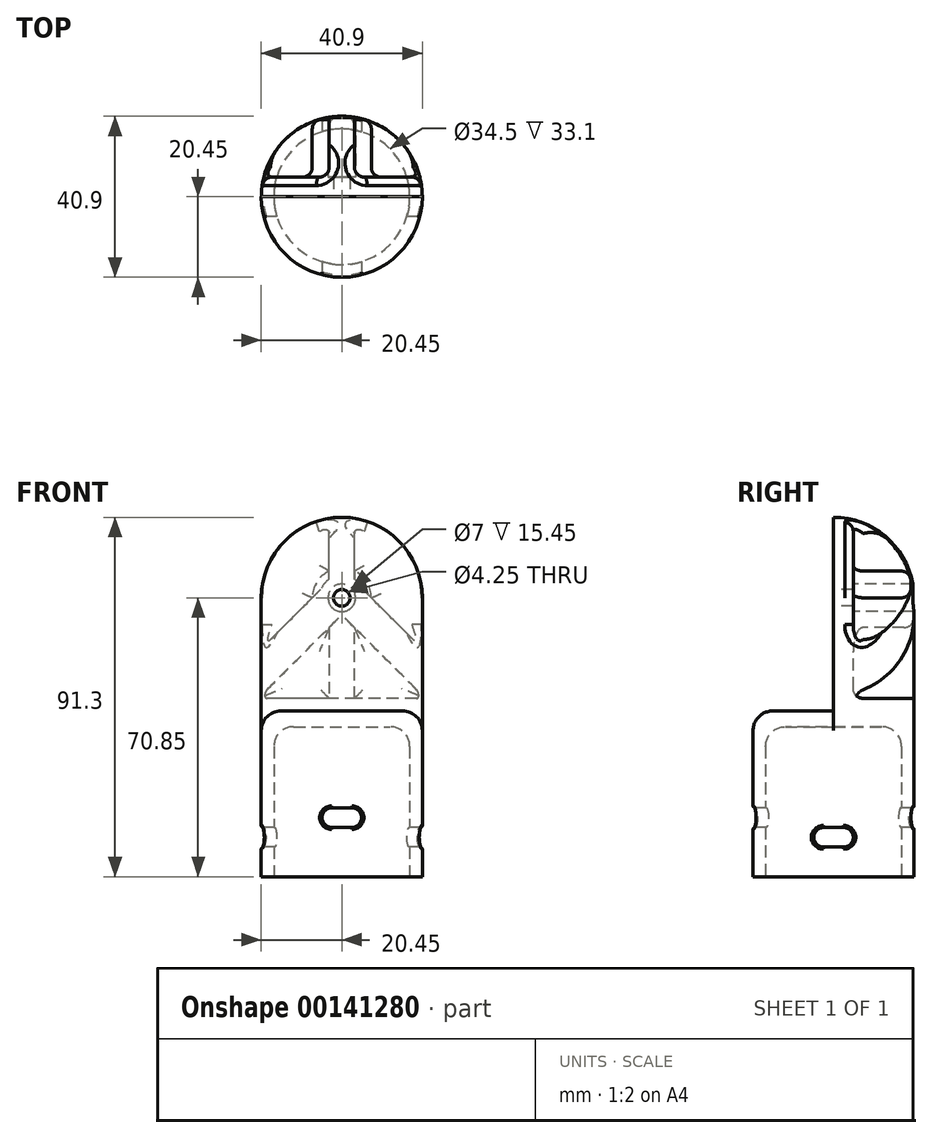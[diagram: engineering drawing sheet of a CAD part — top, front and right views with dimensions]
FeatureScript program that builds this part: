
annotation { "Feature Type Name" : "Feature", "Feature Type Description" : "" }
export const myFeature = defineFeature(function(context is Context, id is Id, definition is map)
    precondition{}
    {
        {
            var Q0;
            Q0=qCreatedBy(makeId("Front.planeOp"),FACE);
            var sketch = newSketch(context, id + "F0", { "sketchPlane" : qUnion([Q0])});
            skLineSegment(sketch, "E0", {"start": v(17.25, 0) * mm, "end": v(17.25, 33.1) * mm});
            skLineSegment(sketch, "E1", {"start": v(12.25, 38.1) * mm, "end": v(0, 38.1) * mm});
            skLineSegment(sketch, "E2", {"start": v(0, 38.1) * mm, "end": v(0, 41.3) * mm});
            skLineSegment(sketch, "E3", {"start": v(0, 41.3) * mm, "end": v(20.45, 41.3) * mm, "construction": true});
            skLineSegment(sketch, "E4", {"start": v(20.45, 41.3) * mm, "end": v(20.45, 0) * mm});
            skLineSegment(sketch, "E5", {"start": v(20.45, 0) * mm, "end": v(17.25, 0) * mm});
            skPoint(sketch, "E6.visualSharp", {"position": v(17.25, 38.1) * mm});
            skArc(sketch, "E6.filletArc", {"start": v(17.25, 33.1) * mm, "mid": v(15.79, 36.64) * mm, "end": v(12.25, 38.1) * mm});
            skLineSegment(sketch, "E7", {"start": v(20.45, 41.3) * mm, "end": v(20.45, 70.85) * mm});
            skLineSegment(sketch, "E8", {"start": v(0, 91.3) * mm, "end": v(0, 91.3) * mm});
            skLineSegment(sketch, "E9", {"start": v(0, 91.3) * mm, "end": v(0, 41.3) * mm});
            skPoint(sketch, "E10.visualSharp", {"position": v(20.45, 91.3) * mm});
            skArc(sketch, "E10.filletArc", {"start": v(20.45, 70.85) * mm, "mid": v(14.46, 85.31) * mm, "end": v(0, 91.3) * mm});
            skSolve(sketch);
        }
        {
            var Q0;
            Q0 = qSketchRegion(id + "F0", true);
            var Q1;
            Q1=sQuery(id+"F0.wireOp",EDGE,"E2");
            revolve(context, id + "F1", {"entities" : qUnion([Q0]), "axis" : qUnion([Q1]), "revolveType" : RevolveType.FULL});
        }
        {
            var Q0;
            Q0=qCreatedBy(makeId("Front.planeOp"),FACE);
            var sketch = newSketch(context, id + "F2", { "sketchPlane" : qUnion([Q0])});
            skArc(sketch, "E11", {"start": v(20.45, 70.85) * mm, "mid": v(0, 91.3) * mm, "end": v(-20.45, 70.85) * mm});
            skLineSegment(sketch, "E12", {"start": v(-20.45, 70.85) * mm, "end": v(-20.45, 42.1) * mm});
            skLineSegment(sketch, "E13", {"start": v(-20.45, 42.1) * mm, "end": v(20.45, 42.1) * mm});
            skLineSegment(sketch, "E14", {"start": v(20.45, 42.1) * mm, "end": v(20.45, 70.85) * mm});
            skSolve(sketch);
        }
        {
            var Q0;
            Q0 = qSketchRegion(id + "F2", true);
            extrude(context, id + "F3", {"entities" : qUnion([Q0]), "operationType" : NewBodyOperationType.REMOVE, "depth" : 25 * mm});
        }
        {
            var Q0;
            Q0=qCreatedBy(makeId("Front.planeOp"),FACE);
            cPlane(context, id + "F4", {"entities" : qUnion([Q0]), "cplaneType" : CPlaneType.OFFSET, "offset" : 5 * mm, "oppositeDirection" : true, "width" : 150 * mm, "height" : 150 * mm});
        }
        {
            var Q0;
            Q0=makeQuery(id+"F3.boolean.opBoolean","INTERSECT",EDGE,{"derivedFrom":[makeQuery(id+"F1.opRevolve","SWEPT_FACE",FACE,{"disambiguationData":[OSD([sQuery(id+"F0.wireOp",EDGE,"E4"),sQuery(id+"F0.wireOp",EDGE,"E7")])]}),makeQuery(id+"F3.opExtrude","SWEPT_FACE",FACE,{"disambiguationData":[OSD([sQuery(id+"F2.wireOp",EDGE,"E13")])]})]});
            fillet(context, id + "F5", {"entities" : qUnion([Q0]), "radius" : 5 * mm, "tangentPropagation" : true, "allowEdgeOverflow" : false});
        }
        {
            var Q0;
            Q0=qCreatedBy(makeId("Front.planeOp"),FACE);
            var sketch = newSketch(context, id + "F6", { "sketchPlane" : qUnion([Q0])});
            skLineSegment(sketch, "E15.bottom", {"start": v(2.5, 12.5) * mm, "end": v(-2.5, 12.5) * mm});
            skLineSegment(sketch, "E15.top", {"start": v(2.5, 17.5) * mm, "end": v(-2.5, 17.5) * mm});
            skLineSegment(sketch, "E15.left", {"start": v(5, 15) * mm, "end": v(5, 15) * mm});
            skLineSegment(sketch, "E15.right", {"start": v(-5, 15) * mm, "end": v(-5, 15) * mm});
            skPoint(sketch, "E15.middle", {"position": v(0, 15) * mm});
            skPoint(sketch, "E16.visualSharp", {"position": v(-5, 17.5) * mm});
            skArc(sketch, "E16.filletArc", {"start": v(-2.5, 17.5) * mm, "mid": v(-4.27, 16.77) * mm, "end": v(-5, 15) * mm});
            skPoint(sketch, "E17.visualSharp", {"position": v(-5, 12.5) * mm});
            skArc(sketch, "E17.filletArc", {"start": v(-5, 15) * mm, "mid": v(-4.27, 13.23) * mm, "end": v(-2.5, 12.5) * mm});
            skPoint(sketch, "E18.visualSharp", {"position": v(5, 12.5) * mm});
            skArc(sketch, "E18.filletArc", {"start": v(2.5, 12.5) * mm, "mid": v(4.27, 13.23) * mm, "end": v(5, 15) * mm});
            skPoint(sketch, "E19.visualSharp", {"position": v(5, 17.5) * mm});
            skArc(sketch, "E19.filletArc", {"start": v(5, 15) * mm, "mid": v(4.27, 16.77) * mm, "end": v(2.5, 17.5) * mm});
            skSolve(sketch);
        }
        {
            var Q0;
            Q0 = qSketchRegion(id + "F6", true);
            extrude(context, id + "F7", {"entities" : qUnion([Q0]), "operationType" : NewBodyOperationType.REMOVE, "endBound" : BoundingType.SYMMETRIC, "oppositeDirection" : true, "depth" : 60 * mm});
        }
        {
            var Q0;
            Q0=qCreatedBy(makeId("Right.planeOp"),FACE);
            var sketch = newSketch(context, id + "F8", { "sketchPlane" : qUnion([Q0])});
            skLineSegment(sketch, "E20.bottom", {"start": v(2.5, 7.5) * mm, "end": v(-2.5, 7.5) * mm});
            skLineSegment(sketch, "E20.top", {"start": v(2.5, 12.5) * mm, "end": v(-2.5, 12.5) * mm});
            skLineSegment(sketch, "E20.left", {"start": v(5, 10) * mm, "end": v(5, 10) * mm});
            skLineSegment(sketch, "E20.right", {"start": v(-5, 10) * mm, "end": v(-5, 10) * mm});
            skPoint(sketch, "E20.middle", {"position": v(0, 10) * mm});
            skPoint(sketch, "E21.visualSharp", {"position": v(-5, 12.5) * mm});
            skArc(sketch, "E21.filletArc", {"start": v(-2.5, 12.5) * mm, "mid": v(-4.27, 11.77) * mm, "end": v(-5, 10) * mm});
            skPoint(sketch, "E22.visualSharp", {"position": v(5, 12.5) * mm});
            skArc(sketch, "E22.filletArc", {"start": v(5, 10) * mm, "mid": v(4.27, 11.77) * mm, "end": v(2.5, 12.5) * mm});
            skPoint(sketch, "E23.visualSharp", {"position": v(5, 7.5) * mm});
            skArc(sketch, "E23.filletArc", {"start": v(2.5, 7.5) * mm, "mid": v(4.27, 8.23) * mm, "end": v(5, 10) * mm});
            skPoint(sketch, "E24.visualSharp", {"position": v(-5, 7.5) * mm});
            skArc(sketch, "E24.filletArc", {"start": v(-5, 10) * mm, "mid": v(-4.27, 8.23) * mm, "end": v(-2.5, 7.5) * mm});
            skSolve(sketch);
        }
        {
            var Q0;
            Q0 = qSketchRegion(id + "F8", true);
            extrude(context, id + "F9", {"entities" : qUnion([Q0]), "operationType" : NewBodyOperationType.REMOVE, "endBound" : BoundingType.SYMMETRIC, "depth" : 60 * mm});
        }
        {
            var Q0;
            Q0=qCreatedBy(id+"F4.planeOp",FACE);
            var sketch = newSketch(context, id + "F10", { "sketchPlane" : qUnion([Q0])});
            skArc(sketch, "E25", {"start": v(-20.2, 70.85) * mm, "mid": v(-15.37, 83.95) * mm, "end": v(-3.2, 90.8) * mm});
            skLineSegment(sketch, "E26", {"start": v(20.2, 70.85) * mm, "end": v(20.2, 58.15) * mm});
            skLineSegment(sketch, "E27", {"start": v(20.2, 45.3) * mm, "end": v(-20.2, 45.3) * mm});
            skLineSegment(sketch, "E28", {"start": v(-20.2, 58.15) * mm, "end": v(-20.2, 70.85) * mm});
            skArc(sketch, "E29", {"start": v(7.5, 70.85) * mm, "mid": v(6.33, 74.87) * mm, "end": v(3.2, 77.63) * mm});
            skLineSegment(sketch, "E30.bottom", {"start": v(3.2, 45.3) * mm, "end": v(-3.2, 45.3) * mm});
            skLineSegment(sketch, "E30.left", {"start": v(3.2, 45.3) * mm, "end": v(3.2, 63.3) * mm});
            skLineSegment(sketch, "E30.right", {"start": v(-3.2, 45.3) * mm, "end": v(-3.2, 63.3) * mm});
            skLineSegment(sketch, "E31", {"start": v(-20.2, 58.15) * mm, "end": v(-7.5, 70.85) * mm});
            skLineSegment(sketch, "E32", {"start": v(20.2, 58.15) * mm, "end": v(7.5, 70.85) * mm});
            skLineSegment(sketch, "E33", {"start": v(3.2, 77.63) * mm, "end": v(3.2, 90.8) * mm});
            skLineSegment(sketch, "E34", {"start": v(-3.2, 77.63) * mm, "end": v(-3.2, 90.8) * mm});
            skArc(sketch, "E35.trimOffspring", {"start": v(-3.2, 77.63) * mm, "mid": v(-6.33, 74.87) * mm, "end": v(-7.5, 70.85) * mm});
            skArc(sketch, "E36.trimOffspring", {"start": v(3.2, 90.8) * mm, "mid": v(15.37, 83.95) * mm, "end": v(20.2, 70.85) * mm});
            skLineSegment(sketch, "E37", {"start": v(20.2, 45.3) * mm, "end": v(20.2, 46.3) * mm});
            skLineSegment(sketch, "E38", {"start": v(20.2, 46.3) * mm, "end": v(3.2, 63.3) * mm});
            skLineSegment(sketch, "E39", {"start": v(-20.2, 45.3) * mm, "end": v(-20.2, 46.3) * mm});
            skLineSegment(sketch, "E40", {"start": v(-20.2, 46.3) * mm, "end": v(-3.2, 63.3) * mm});
            skCircle(sketch, "E41", {"center": v(0, 70.85) * mm, "radius": 3.5 * mm});
            skSolve(sketch);
        }
        {
            var Q0;
            Q0 = qSketchRegion(id + "F10", true);
            extrude(context, id + "F11", {"entities" : qUnion([Q0]), "operationType" : NewBodyOperationType.REMOVE, "endBound" : BoundingType.THROUGH_ALL, "oppositeDirection" : true, "depth" : 25 * mm});
        }
        {
            var Q0;
            Q0=makeQuery(id+"F3.boolean.opBoolean","COPY",FACE,{"derivedFrom":makeQuery(id+"F3.opExtrude","CAP_FACE",FACE,{"disambiguationData":[OSD([sQuery(id+"F2.wireOp",EDGE,"E11"),sQuery(id+"F2.wireOp",EDGE,"E12"),sQuery(id+"F2.wireOp",EDGE,"E13"),sQuery(id+"F2.wireOp",EDGE,"E14")])],"isStart":true})});
            var sketch = newSketch(context, id + "F12", { "sketchPlane" : qUnion([Q0])});
            skCircle(sketch, "E42", {"center": v(0, 70.85) * mm, "radius": 2.12 * mm});
            skSolve(sketch);
        }
        {
            var Q0;
            Q0 = qSketchRegion(id + "F12", true);
            extrude(context, id + "F13", {"entities" : qUnion([Q0]), "operationType" : NewBodyOperationType.REMOVE, "endBound" : BoundingType.THROUGH_ALL, "oppositeDirection" : true, "depth" : 25 * mm});
        }
        {
            var Q0;
            Q0=makeQuery(id+"F11.boolean.opBoolean","COPY",FACE,{"derivedFrom":makeQuery(id+"F11.opExtrude","CAP_FACE",FACE,{"disambiguationData":[OSD([sQuery(id+"F10.wireOp",EDGE,"E26"),sQuery(id+"F10.wireOp",EDGE,"E29"),sQuery(id+"F10.wireOp",EDGE,"E32"),sQuery(id+"F10.wireOp",EDGE,"E33"),sQuery(id+"F10.wireOp",EDGE,"E36.trimOffspring")])],"isStart":true})});
            var Q1;
            Q1=makeQuery(id+"F11.boolean.opBoolean","COPY",FACE,{"derivedFrom":makeQuery(id+"F11.opExtrude","CAP_FACE",FACE,{"disambiguationData":[OSD([sQuery(id+"F10.wireOp",EDGE,"E25"),sQuery(id+"F10.wireOp",EDGE,"E28"),sQuery(id+"F10.wireOp",EDGE,"E31"),sQuery(id+"F10.wireOp",EDGE,"E34"),sQuery(id+"F10.wireOp",EDGE,"E35.trimOffspring")])],"isStart":true})});
            var Q2;
            Q2=makeQuery(id+"F11.boolean.opBoolean","INTERSECT",EDGE,{"derivedFrom":[makeQuery(id+"F1.opRevolve","SWEPT_FACE",FACE,{"disambiguationData":[OSD([sQuery(id+"F0.wireOp",EDGE,"E10.filletArc")])]}),makeQuery(id+"F11.opExtrude","SWEPT_FACE",FACE,{"disambiguationData":[OSD([sQuery(id+"F10.wireOp",EDGE,"E29")])]})]});
            var Q3;
            Q3=makeQuery(id+"F11.boolean.opBoolean","INTERSECT",EDGE,{"derivedFrom":[makeQuery(id+"F1.opRevolve","SWEPT_FACE",FACE,{"disambiguationData":[OSD([sQuery(id+"F0.wireOp",EDGE,"E10.filletArc")])]}),makeQuery(id+"F11.opExtrude","SWEPT_FACE",FACE,{"disambiguationData":[OSD([sQuery(id+"F10.wireOp",EDGE,"E35.trimOffspring")])]})]});
            var Q4;
            Q4=makeQuery(id+"F11.boolean.opBoolean","COPY",FACE,{"derivedFrom":makeQuery(id+"F11.opExtrude","CAP_FACE",FACE,{"disambiguationData":[OSD([sQuery(id+"F10.wireOp",EDGE,"E27"),sQuery(id+"F10.wireOp",EDGE,"E30.left"),sQuery(id+"F10.wireOp",EDGE,"E37"),sQuery(id+"F10.wireOp",EDGE,"E38")])],"isStart":true})});
            var Q5;
            Q5=makeQuery(id+"F11.boolean.opBoolean","COPY",FACE,{"derivedFrom":makeQuery(id+"F11.opExtrude","CAP_FACE",FACE,{"disambiguationData":[OSD([sQuery(id+"F10.wireOp",EDGE,"E27"),sQuery(id+"F10.wireOp",EDGE,"E30.right"),sQuery(id+"F10.wireOp",EDGE,"E39"),sQuery(id+"F10.wireOp",EDGE,"E40")])],"isStart":true})});
            var Q6;
            Q6=makeQuery(id+"F11.boolean.opBoolean","INTERSECT",EDGE,{"derivedFrom":[makeQuery(id+"F1.opRevolve","SWEPT_FACE",FACE,{"disambiguationData":[OSD([sQuery(id+"F0.wireOp",EDGE,"E4"),sQuery(id+"F0.wireOp",EDGE,"E7")])]}),makeQuery(id+"F11.opExtrude","SWEPT_FACE",FACE,{"disambiguationData":[OSD([sQuery(id+"F10.wireOp",EDGE,"E30.right")])]})]});
            var Q7;
            Q7=makeQuery(id+"F11.boolean.opBoolean","INTERSECT",EDGE,{"derivedFrom":[makeQuery(id+"F1.opRevolve","SWEPT_FACE",FACE,{"disambiguationData":[OSD([sQuery(id+"F0.wireOp",EDGE,"E4"),sQuery(id+"F0.wireOp",EDGE,"E7")])]}),makeQuery(id+"F11.opExtrude","SWEPT_FACE",FACE,{"disambiguationData":[OSD([sQuery(id+"F10.wireOp",EDGE,"E30.left")])]})]});
            fillet(context, id + "F14", {"entities" : qUnion([Q0, Q1, Q2, Q3, Q4, Q5, Q6, Q7]), "radius" : 2.5 * mm, "tangentPropagation" : true, "allowEdgeOverflow" : false});
        }
        {
            var Q0;
            Q0=makeQuery(id+"F9.boolean.opBoolean","INTERSECT",EDGE,{"disambiguationData":[OD(1.0)],"derivedFrom":[makeQuery(id+"F1.opRevolve","SWEPT_FACE",FACE,{"disambiguationData":[OSD([sQuery(id+"F0.wireOp",EDGE,"E4"),sQuery(id+"F0.wireOp",EDGE,"E7")])]}),makeQuery(id+"F9.opExtrude","SWEPT_FACE",FACE,{"disambiguationData":[OSD([sQuery(id+"F8.wireOp",EDGE,"E22.filletArc"),sQuery(id+"F8.wireOp",EDGE,"E23.filletArc")])]})]});
            var Q1;
            Q1=makeQuery(id+"F9.boolean.opBoolean","INTERSECT",EDGE,{"disambiguationData":[OD(1.0)],"derivedFrom":[makeQuery(id+"F1.opRevolve","SWEPT_FACE",FACE,{"disambiguationData":[OSD([sQuery(id+"F0.wireOp",EDGE,"E4"),sQuery(id+"F0.wireOp",EDGE,"E7")])]}),makeQuery(id+"F9.opExtrude","SWEPT_FACE",FACE,{"disambiguationData":[OSD([sQuery(id+"F8.wireOp",EDGE,"E20.top")])]})]});
            var Q2;
            Q2=makeQuery(id+"F9.boolean.opBoolean","INTERSECT",EDGE,{"disambiguationData":[OD(1.0)],"derivedFrom":[makeQuery(id+"F1.opRevolve","SWEPT_FACE",FACE,{"disambiguationData":[OSD([sQuery(id+"F0.wireOp",EDGE,"E4"),sQuery(id+"F0.wireOp",EDGE,"E7")])]}),makeQuery(id+"F9.opExtrude","SWEPT_FACE",FACE,{"disambiguationData":[OSD([sQuery(id+"F8.wireOp",EDGE,"E21.filletArc"),sQuery(id+"F8.wireOp",EDGE,"E24.filletArc")])]})]});
            var Q3;
            Q3=makeQuery(id+"F9.boolean.opBoolean","INTERSECT",EDGE,{"disambiguationData":[OD(1.0)],"derivedFrom":[makeQuery(id+"F1.opRevolve","SWEPT_FACE",FACE,{"disambiguationData":[OSD([sQuery(id+"F0.wireOp",EDGE,"E4"),sQuery(id+"F0.wireOp",EDGE,"E7")])]}),makeQuery(id+"F9.opExtrude","SWEPT_FACE",FACE,{"disambiguationData":[OSD([sQuery(id+"F8.wireOp",EDGE,"E20.bottom")])]})]});
            var Q4;
            Q4=makeQuery(id+"F7.boolean.opBoolean","INTERSECT",EDGE,{"disambiguationData":[OD(1.0)],"derivedFrom":[makeQuery(id+"F1.opRevolve","SWEPT_FACE",FACE,{"disambiguationData":[OSD([sQuery(id+"F0.wireOp",EDGE,"E4"),sQuery(id+"F0.wireOp",EDGE,"E7")])]}),makeQuery(id+"F7.opExtrude","SWEPT_FACE",FACE,{"disambiguationData":[OSD([sQuery(id+"F6.wireOp",EDGE,"E15.top")])]})]});
            var Q5;
            Q5=makeQuery(id+"F7.boolean.opBoolean","INTERSECT",EDGE,{"disambiguationData":[OD(1.0)],"derivedFrom":[makeQuery(id+"F1.opRevolve","SWEPT_FACE",FACE,{"disambiguationData":[OSD([sQuery(id+"F0.wireOp",EDGE,"E4"),sQuery(id+"F0.wireOp",EDGE,"E7")])]}),makeQuery(id+"F7.opExtrude","SWEPT_FACE",FACE,{"disambiguationData":[OSD([sQuery(id+"F6.wireOp",EDGE,"E16.filletArc"),sQuery(id+"F6.wireOp",EDGE,"E17.filletArc")])]})]});
            var Q6;
            Q6=makeQuery(id+"F9.boolean.opBoolean","INTERSECT",EDGE,{"disambiguationData":[OD(0.0)],"derivedFrom":[makeQuery(id+"F1.opRevolve","SWEPT_FACE",FACE,{"disambiguationData":[OSD([sQuery(id+"F0.wireOp",EDGE,"E4"),sQuery(id+"F0.wireOp",EDGE,"E7")])]}),makeQuery(id+"F9.opExtrude","SWEPT_FACE",FACE,{"disambiguationData":[OSD([sQuery(id+"F8.wireOp",EDGE,"E21.filletArc"),sQuery(id+"F8.wireOp",EDGE,"E24.filletArc")])]})]});
            var Q7;
            Q7=makeQuery(id+"F7.boolean.opBoolean","INTERSECT",EDGE,{"disambiguationData":[OD(0.0)],"derivedFrom":[makeQuery(id+"F1.opRevolve","SWEPT_FACE",FACE,{"disambiguationData":[OSD([sQuery(id+"F0.wireOp",EDGE,"E4"),sQuery(id+"F0.wireOp",EDGE,"E7")])]}),makeQuery(id+"F7.opExtrude","SWEPT_FACE",FACE,{"disambiguationData":[OSD([sQuery(id+"F6.wireOp",EDGE,"E18.filletArc"),sQuery(id+"F6.wireOp",EDGE,"E19.filletArc")])]})]});
            fillet(context, id + "F15", {"entities" : qUnion([Q0, Q1, Q2, Q3, Q4, Q5, Q6, Q7]), "radius" : .5 * mm, "tangentPropagation" : true, "allowEdgeOverflow" : false});
        }
    });
